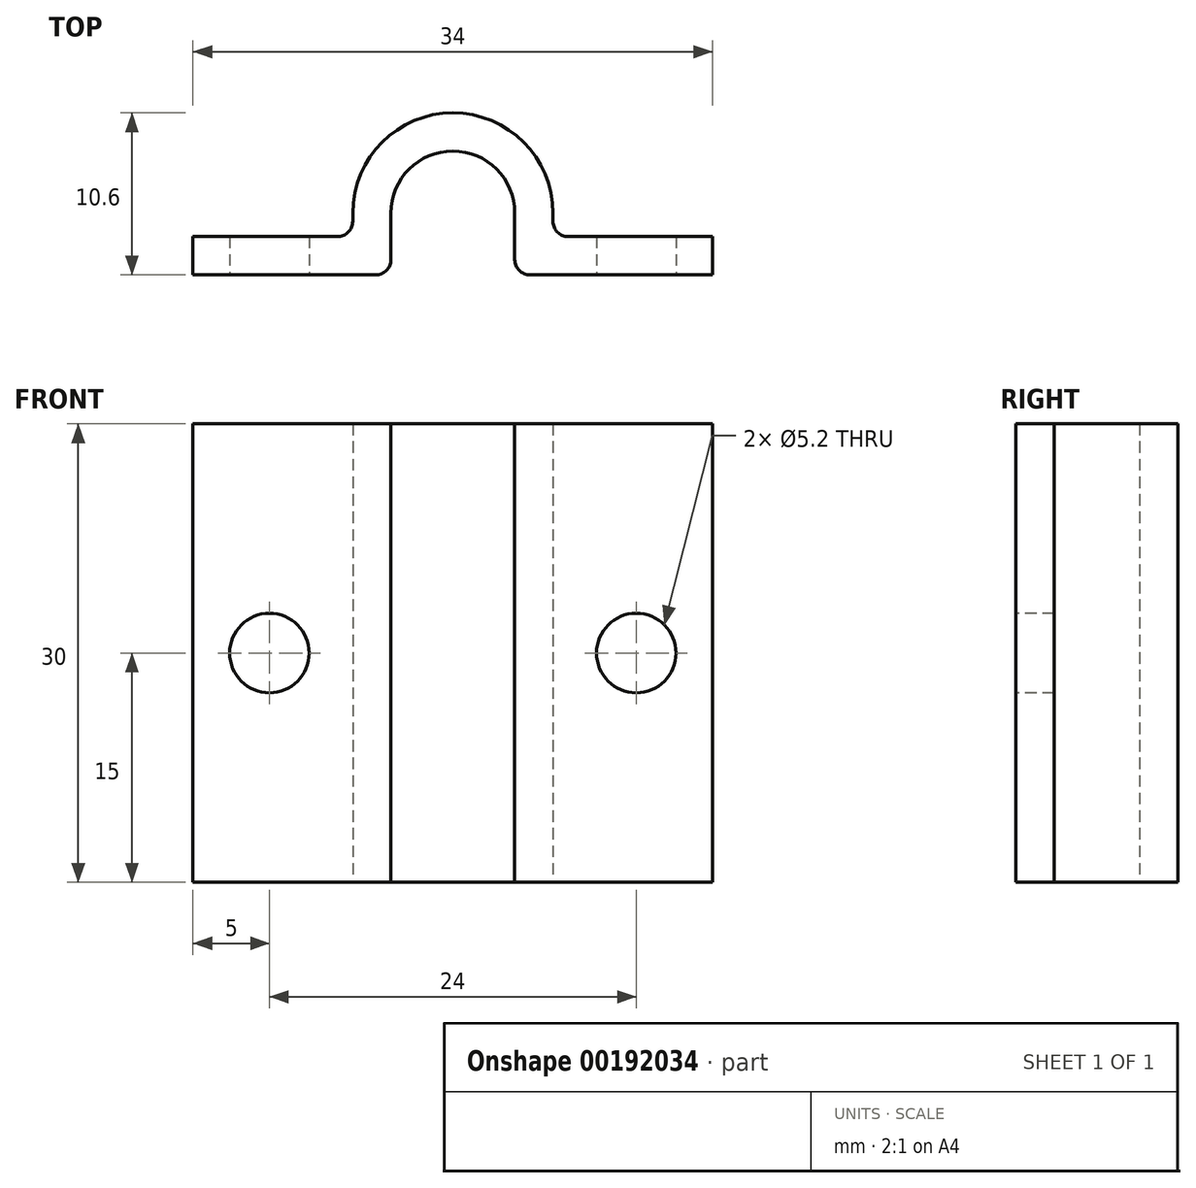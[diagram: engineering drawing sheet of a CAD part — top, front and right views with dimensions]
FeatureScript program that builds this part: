
annotation { "Feature Type Name" : "Feature", "Feature Type Description" : "" }
export const myFeature = defineFeature(function(context is Context, id is Id, definition is map)
    precondition{}
    {
        {
            var Q0;
            Q0=qCreatedBy(makeId("Top.planeOp"),FACE);
            var sketch = newSketch(context, id + "F0", { "sketchPlane" : qUnion([Q0])});
            skCircle(sketch, "E0", {"center": v(0, 4.05) * mm, "radius": 4.05 * mm, "construction": true});
            skArc(sketch, "E1", {"start": v(-4.05, 4.05) * mm, "mid": v(0, 8.1) * mm, "end": v(4.05, 4.05) * mm});
            skLineSegment(sketch, "E2", {"start": v(-4.05, 4.05) * mm, "end": v(-4.05, 0) * mm});
            skLineSegment(sketch, "E3", {"start": v(-4.05, 0) * mm, "end": v(-17, 0) * mm});
            skLineSegment(sketch, "E4", {"start": v(-17, 0) * mm, "end": v(-17, 2.5) * mm});
            skLineSegment(sketch, "E5", {"start": v(-17, 2.5) * mm, "end": v(-6.55, 2.5) * mm});
            skArc(sketch, "E6.0", {"start": v(-6.55, 4.05) * mm, "mid": v(0, 10.6) * mm, "end": v(6.55, 4.05) * mm});
            skLineSegment(sketch, "E7", {"start": v(-6.55, 2.5) * mm, "end": v(-6.55, 4.05) * mm});
            skLineSegment(sketch, "E8.MirrorCS", {"start": v(4.05, 4.05) * mm, "end": v(4.05, 0) * mm});
            skLineSegment(sketch, "E9.MirrorCS", {"start": v(4.05, 0) * mm, "end": v(17, 0) * mm});
            skLineSegment(sketch, "E10.MirrorCS", {"start": v(17, 2.5) * mm, "end": v(6.55, 2.5) * mm});
            skLineSegment(sketch, "E11.MirrorCS", {"start": v(6.55, 2.5) * mm, "end": v(6.55, 4.05) * mm});
            skLineSegment(sketch, "E12.MirrorCS", {"start": v(17, 0) * mm, "end": v(17, 2.5) * mm});
            skSolve(sketch);
        }
        {
            var Q0;
            Q0 = qSketchRegion(id + "F0", true);
            extrude(context, id + "F1", {"entities" : qUnion([Q0]), "depth" : 30 * mm, "symmetric" : true});
        }
        {
            var Q0;
            Q0=makeQuery(id+"F1.opExtrude","SWEPT_FACE",FACE,{"disambiguationData":[OSD([sQuery(id+"F0.wireOp",EDGE,"E3")])]});
            var sketch = newSketch(context, id + "F2", { "sketchPlane" : qUnion([Q0])});
            skCircle(sketch, "E13", {"center": v(-12, 0) * mm, "radius": 2.6 * mm});
            skCircle(sketch, "E14.MirrorC", {"center": v(12, 0) * mm, "radius": 2.6 * mm});
            skSolve(sketch);
        }
        {
            var Q0;
            Q0 = qSketchRegion(id + "F2", true);
            extrude(context, id + "F3", {"entities" : qUnion([Q0]), "operationType" : NewBodyOperationType.REMOVE, "endBound" : BoundingType.THROUGH_ALL, "oppositeDirection" : true, "depth" : 25 * mm});
        }
        {
            var Q0;
            Q0=makeQuery(id+"F1.opExtrude","SWEPT_EDGE",EDGE,{"disambiguationData":[OSD([sQuery(id+"F0.wireOp",EDGE,"E2"),sQuery(id+"F0.wireOp",EDGE,"E3")])]});
            var Q1;
            Q1=makeQuery(id+"F1.opExtrude","SWEPT_EDGE",EDGE,{"disambiguationData":[OSD([sQuery(id+"F0.wireOp",EDGE,"E8.MirrorCS"),sQuery(id+"F0.wireOp",EDGE,"E9.MirrorCS")])]});
            var Q2;
            Q2=makeQuery(id+"F1.opExtrude","SWEPT_EDGE",EDGE,{"disambiguationData":[OSD([sQuery(id+"F0.wireOp",EDGE,"E10.MirrorCS"),sQuery(id+"F0.wireOp",EDGE,"E11.MirrorCS")])]});
            var Q3;
            Q3=makeQuery(id+"F1.opExtrude","SWEPT_EDGE",EDGE,{"disambiguationData":[OSD([sQuery(id+"F0.wireOp",EDGE,"E5"),sQuery(id+"F0.wireOp",EDGE,"E7")])]});
            fillet(context, id + "F4", {"entities" : qUnion([Q0, Q1, Q2, Q3]), "radius" : 1 * mm, "allowEdgeOverflow" : false});
        }
    });
